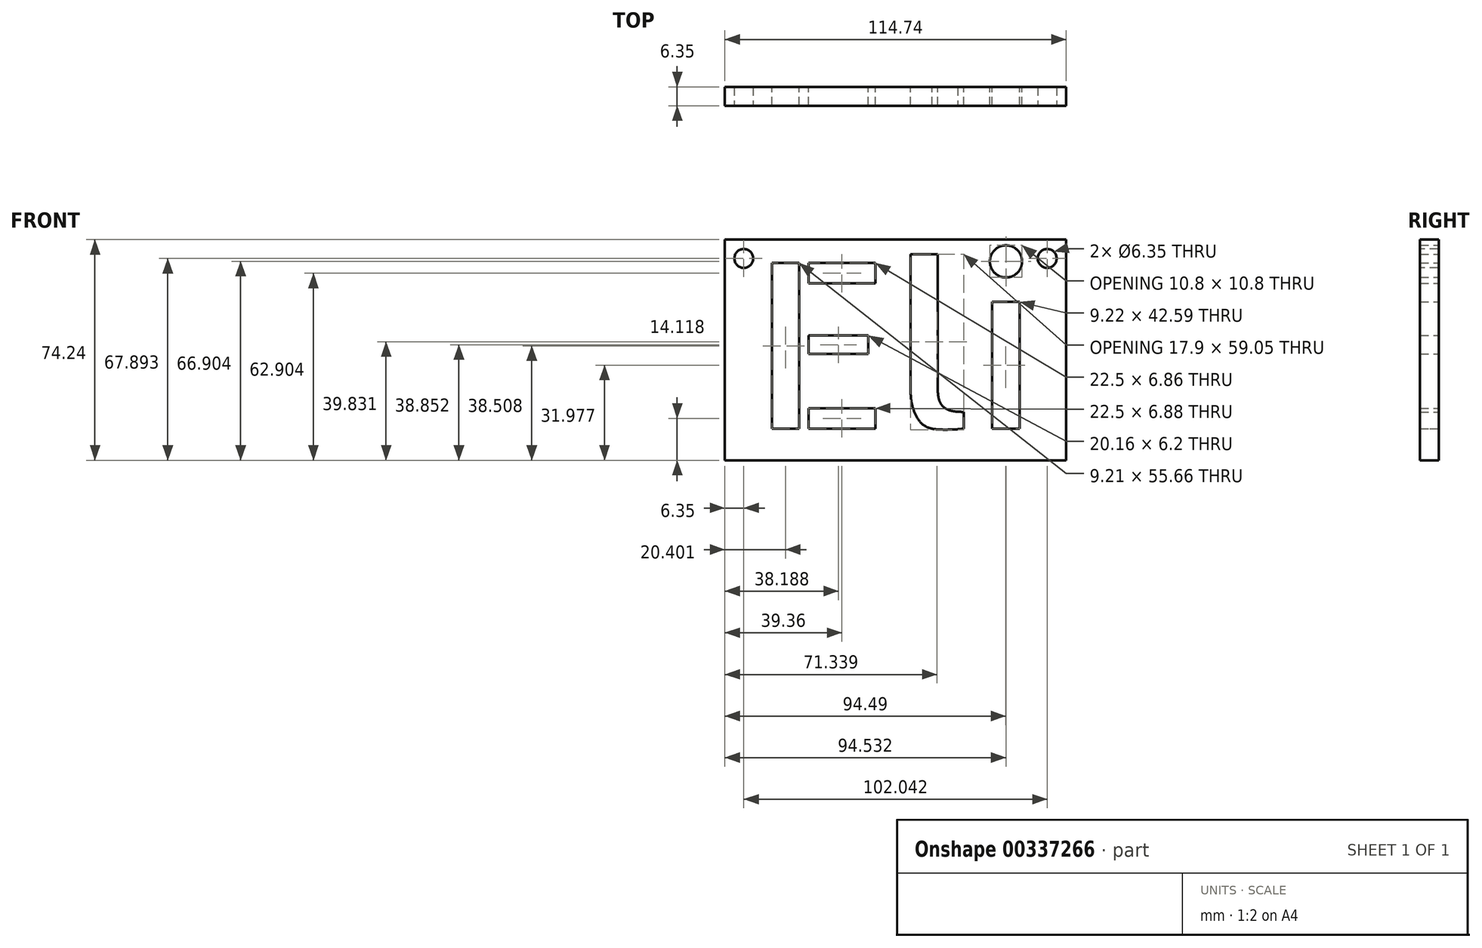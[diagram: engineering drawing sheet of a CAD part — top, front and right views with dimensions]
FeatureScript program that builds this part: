
annotation { "Feature Type Name" : "Feature", "Feature Type Description" : "" }
export const myFeature = defineFeature(function(context is Context, id is Id, definition is map)
    precondition{}
    {
        {
            var Q0;
            Q0=qCreatedBy(makeId("Front.planeOp"),FACE);
            var sketch = newSketch(context, id + "F0", { "sketchPlane" : qUnion([Q0])});
            skText(sketch, "E0", { "text": "Eli \n", "fontName": "AllertaStencil-Regular.ttf"});
            skLineSegment(sketch, "E1.bottom", {"start": v(-54.84, 32.76) * mm, "end": v(59.9, 32.76) * mm});
            skLineSegment(sketch, "E1.top", {"start": v(-54.84, -41.48) * mm, "end": v(59.9, -41.48) * mm});
            skLineSegment(sketch, "E1.left", {"start": v(-54.84, 32.76) * mm, "end": v(-54.84, -41.48) * mm});
            skLineSegment(sketch, "E1.right", {"start": v(59.9, 32.76) * mm, "end": v(59.9, -41.48) * mm});
            const initialGuessF0  = {"E0": [-0.04622, -0.0308, 1, 0, 0.05568]};
            skSetInitialGuess(sketch, initialGuessF0);
            skSolve(sketch);
        }
        {
            var Q0;
            Q0 = qSketchRegion(id + "F0", true);
            extrude(context, id + "F1", {"entities" : qUnion([Q0]), "depth" : 6.35 * mm});
        }
        {
            var Q0;
            Q0=makeQuery(id+"F1.opExtrude","CAP_FACE",FACE,{"disambiguationData":[OSD([sQuery(id+"F0.wireOp",EDGE,"E0.sketch_text.stroke-0"),sQuery(id+"F0.wireOp",EDGE,"E0.sketch_text.stroke-1"),sQuery(id+"F0.wireOp",EDGE,"E0.sketch_text.stroke-2"),sQuery(id+"F0.wireOp",EDGE,"E0.sketch_text.stroke-3"),sQuery(id+"F0.wireOp",EDGE,"E0.sketch_text.stroke-4"),sQuery(id+"F0.wireOp",EDGE,"E0.sketch_text.stroke-5"),sQuery(id+"F0.wireOp",EDGE,"E0.sketch_text.stroke-6"),sQuery(id+"F0.wireOp",EDGE,"E0.sketch_text.stroke-7"),sQuery(id+"F0.wireOp",EDGE,"E0.sketch_text.stroke-8"),sQuery(id+"F0.wireOp",EDGE,"E0.sketch_text.stroke-9"),sQuery(id+"F0.wireOp",EDGE,"E0.sketch_text.stroke-10"),sQuery(id+"F0.wireOp",EDGE,"E0.sketch_text.stroke-11"),sQuery(id+"F0.wireOp",EDGE,"E0.sketch_text.stroke-12"),sQuery(id+"F0.wireOp",EDGE,"E0.sketch_text.stroke-13"),sQuery(id+"F0.wireOp",EDGE,"E0.sketch_text.stroke-14"),sQuery(id+"F0.wireOp",EDGE,"E0.sketch_text.stroke-15"),sQuery(id+"F0.wireOp",EDGE,"E0.sketch_text.stroke-16"),sQuery(id+"F0.wireOp",EDGE,"E0.sketch_text.stroke-17"),sQuery(id+"F0.wireOp",EDGE,"E0.sketch_text.stroke-18"),sQuery(id+"F0.wireOp",EDGE,"E0.sketch_text.stroke-19"),sQuery(id+"F0.wireOp",EDGE,"E0.sketch_text.stroke-20"),sQuery(id+"F0.wireOp",EDGE,"E0.sketch_text.stroke-21"),sQuery(id+"F0.wireOp",EDGE,"E0.sketch_text.stroke-22"),sQuery(id+"F0.wireOp",EDGE,"E0.sketch_text.stroke-23"),sQuery(id+"F0.wireOp",EDGE,"E0.sketch_text.stroke-24"),sQuery(id+"F0.wireOp",EDGE,"E0.sketch_text.stroke-25"),sQuery(id+"F0.wireOp",EDGE,"E0.sketch_text.stroke-26"),sQuery(id+"F0.wireOp",EDGE,"E0.sketch_text.stroke-27"),sQuery(id+"F0.wireOp",EDGE,"E0.sketch_text.stroke-28"),sQuery(id+"F0.wireOp",EDGE,"E0.sketch_text.stroke-29"),sQuery(id+"F0.wireOp",EDGE,"E0.sketch_text.stroke-30"),sQuery(id+"F0.wireOp",EDGE,"E0.sketch_text.stroke-31"),sQuery(id+"F0.wireOp",EDGE,"E0.sketch_text.stroke-32"),sQuery(id+"F0.wireOp",EDGE,"E0.sketch_text.stroke-33"),sQuery(id+"F0.wireOp",EDGE,"E0.sketch_text.stroke-34"),sQuery(id+"F0.wireOp",EDGE,"E0.sketch_text.stroke-35"),sQuery(id+"F0.wireOp",EDGE,"E0.sketch_text.stroke-36"),sQuery(id+"F0.wireOp",EDGE,"E0.sketch_text.stroke-37"),sQuery(id+"F0.wireOp",EDGE,"E0.sketch_text.stroke-38"),sQuery(id+"F0.wireOp",EDGE,"E0.sketch_text.stroke-39"),sQuery(id+"F0.wireOp",EDGE,"E0.sketch_text.stroke-40"),sQuery(id+"F0.wireOp",EDGE,"E0.sketch_text.stroke-41"),sQuery(id+"F0.wireOp",EDGE,"E0.sketch_text.stroke-42"),sQuery(id+"F0.wireOp",EDGE,"E0.sketch_text.stroke-43"),sQuery(id+"F0.wireOp",EDGE,"E0.sketch_text.stroke-44"),sQuery(id+"F0.wireOp",EDGE,"E0.sketch_text.stroke-45"),sQuery(id+"F0.wireOp",EDGE,"E1.bottom"),sQuery(id+"F0.wireOp",EDGE,"E1.top"),sQuery(id+"F0.wireOp",EDGE,"E1.left"),sQuery(id+"F0.wireOp",EDGE,"E1.right")])],"isStart":false});
            var sketch = newSketch(context, id + "F2", { "sketchPlane" : qUnion([Q0])});
            skPoint(sketch, "E2", {"position": v(-48.49, 26.41) * mm});
            skPoint(sketch, "E3", {"position": v(53.55, 26.41) * mm});
            skSolve(sketch);
        }
        {
            var Q0;
            Q0=sQuery(id+"F2.wireOp",VERTEX,"E2");
            var Q1;
            Q1=sQuery(id+"F2.wireOp",VERTEX,"E3");
            var Q2;
            Q2=makeQuery(id+"F1.opExtrude","SWEPT_BODY",BODY,{"disambiguationData":[OSD([sQuery(id+"F0.wireOp",EDGE,"E0.sketch_text.stroke-0"),sQuery(id+"F0.wireOp",EDGE,"E0.sketch_text.stroke-1"),sQuery(id+"F0.wireOp",EDGE,"E0.sketch_text.stroke-2"),sQuery(id+"F0.wireOp",EDGE,"E0.sketch_text.stroke-3"),sQuery(id+"F0.wireOp",EDGE,"E0.sketch_text.stroke-4"),sQuery(id+"F0.wireOp",EDGE,"E0.sketch_text.stroke-5"),sQuery(id+"F0.wireOp",EDGE,"E0.sketch_text.stroke-6"),sQuery(id+"F0.wireOp",EDGE,"E0.sketch_text.stroke-7"),sQuery(id+"F0.wireOp",EDGE,"E0.sketch_text.stroke-8"),sQuery(id+"F0.wireOp",EDGE,"E0.sketch_text.stroke-9"),sQuery(id+"F0.wireOp",EDGE,"E0.sketch_text.stroke-10"),sQuery(id+"F0.wireOp",EDGE,"E0.sketch_text.stroke-11"),sQuery(id+"F0.wireOp",EDGE,"E0.sketch_text.stroke-12"),sQuery(id+"F0.wireOp",EDGE,"E0.sketch_text.stroke-13"),sQuery(id+"F0.wireOp",EDGE,"E0.sketch_text.stroke-14"),sQuery(id+"F0.wireOp",EDGE,"E0.sketch_text.stroke-15"),sQuery(id+"F0.wireOp",EDGE,"E0.sketch_text.stroke-16"),sQuery(id+"F0.wireOp",EDGE,"E0.sketch_text.stroke-17"),sQuery(id+"F0.wireOp",EDGE,"E0.sketch_text.stroke-18"),sQuery(id+"F0.wireOp",EDGE,"E0.sketch_text.stroke-19"),sQuery(id+"F0.wireOp",EDGE,"E0.sketch_text.stroke-20"),sQuery(id+"F0.wireOp",EDGE,"E0.sketch_text.stroke-21"),sQuery(id+"F0.wireOp",EDGE,"E0.sketch_text.stroke-22"),sQuery(id+"F0.wireOp",EDGE,"E0.sketch_text.stroke-23"),sQuery(id+"F0.wireOp",EDGE,"E0.sketch_text.stroke-24"),sQuery(id+"F0.wireOp",EDGE,"E0.sketch_text.stroke-25"),sQuery(id+"F0.wireOp",EDGE,"E0.sketch_text.stroke-26"),sQuery(id+"F0.wireOp",EDGE,"E0.sketch_text.stroke-27"),sQuery(id+"F0.wireOp",EDGE,"E0.sketch_text.stroke-28"),sQuery(id+"F0.wireOp",EDGE,"E0.sketch_text.stroke-29"),sQuery(id+"F0.wireOp",EDGE,"E0.sketch_text.stroke-30"),sQuery(id+"F0.wireOp",EDGE,"E0.sketch_text.stroke-31"),sQuery(id+"F0.wireOp",EDGE,"E0.sketch_text.stroke-32"),sQuery(id+"F0.wireOp",EDGE,"E0.sketch_text.stroke-33"),sQuery(id+"F0.wireOp",EDGE,"E0.sketch_text.stroke-34"),sQuery(id+"F0.wireOp",EDGE,"E0.sketch_text.stroke-35"),sQuery(id+"F0.wireOp",EDGE,"E0.sketch_text.stroke-36"),sQuery(id+"F0.wireOp",EDGE,"E0.sketch_text.stroke-37"),sQuery(id+"F0.wireOp",EDGE,"E0.sketch_text.stroke-38"),sQuery(id+"F0.wireOp",EDGE,"E0.sketch_text.stroke-39"),sQuery(id+"F0.wireOp",EDGE,"E0.sketch_text.stroke-40"),sQuery(id+"F0.wireOp",EDGE,"E0.sketch_text.stroke-41"),sQuery(id+"F0.wireOp",EDGE,"E0.sketch_text.stroke-42"),sQuery(id+"F0.wireOp",EDGE,"E0.sketch_text.stroke-43"),sQuery(id+"F0.wireOp",EDGE,"E0.sketch_text.stroke-44"),sQuery(id+"F0.wireOp",EDGE,"E0.sketch_text.stroke-45"),sQuery(id+"F0.wireOp",EDGE,"E1.bottom"),sQuery(id+"F0.wireOp",EDGE,"E1.top"),sQuery(id+"F0.wireOp",EDGE,"E1.left"),sQuery(id+"F0.wireOp",EDGE,"E1.right")])]});
            hole(context, id + "F3", {"style" : HoleStyle.SIMPLE, "endStyle" : HoleEndStyle.THROUGH, "holeDiameter" : 6.35 * mm, "isTappedThrough" : true, "tappedDepth" : 12.7 * mm, "tapClearance" : 3, "locations" : qUnion([Q0, Q1]), "scope" : qUnion([Q2])});
        }
    });
